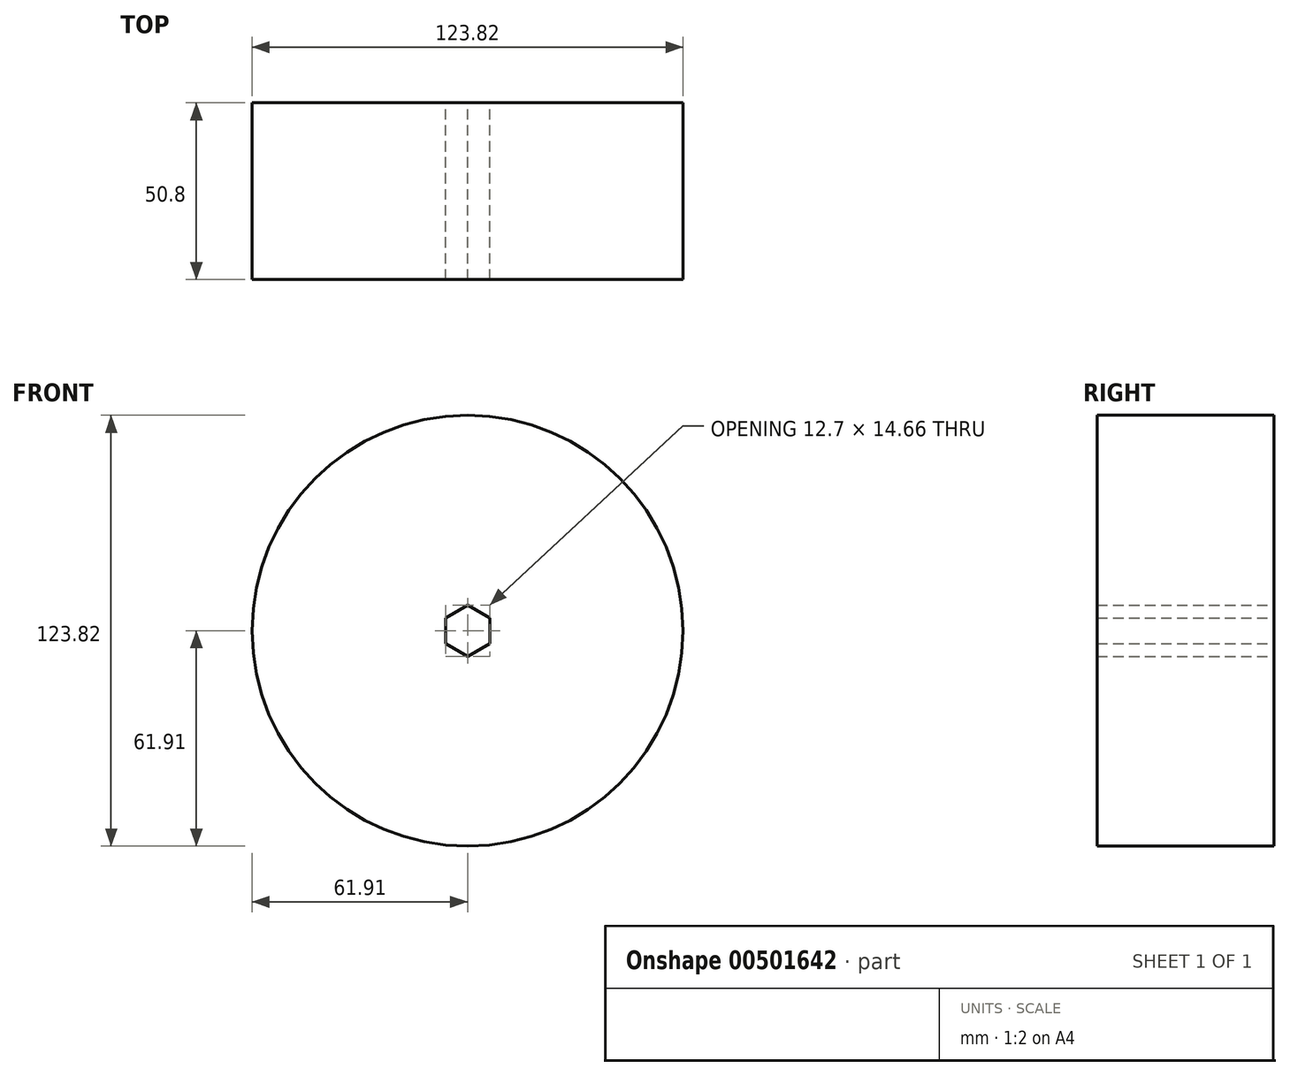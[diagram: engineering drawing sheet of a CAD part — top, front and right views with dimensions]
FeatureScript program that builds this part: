
annotation { "Feature Type Name" : "Feature", "Feature Type Description" : "" }
export const myFeature = defineFeature(function(context is Context, id is Id, definition is map)
    precondition{}
    {
        {
            var Q0;
            Q0=qCreatedBy(makeId("Front.planeOp"),FACE);
            var sketch = newSketch(context, id + "F0", { "sketchPlane" : qUnion([Q0])});
            skCircle(sketch, "E0", {"center": v(0, 0) * mm, "radius": 61.91 * mm});
            skCircle(sketch, "E1.cCircle", {"center": v(0, 0) * mm, "radius": 6.35 * mm, "construction": true});
            skLineSegment(sketch, "E1.0", {"start": v(-6.35, -3.67) * mm, "end": v(-6.35, 3.67) * mm});
            skLineSegment(sketch, "E1.1", {"start": v(-6.35, 3.67) * mm, "end": v(0, 7.33) * mm});
            skLineSegment(sketch, "E1.2", {"start": v(0, 7.33) * mm, "end": v(6.35, 3.67) * mm});
            skLineSegment(sketch, "E1.3", {"start": v(6.35, 3.67) * mm, "end": v(6.35, -3.67) * mm});
            skLineSegment(sketch, "E1.4", {"start": v(6.35, -3.67) * mm, "end": v(0, -7.33) * mm});
            skLineSegment(sketch, "E1.5", {"start": v(0, -7.33) * mm, "end": v(-6.35, -3.67) * mm});
            skPoint(sketch, "E1.0.midPoint", {"position": v(-6.35, 0) * mm});
            skSolve(sketch);
        }
        {
            var Q0;
            Q0=makeQuery(id+"F0.imprint","IMPRINT",FACE,{"disambiguationData":[TD([[makeQuery(id+"F0.imprint","IMPRINT",EDGE,{"derivedFrom":sQuery(id+"F0.wireOp",EDGE,"E0")}),1.0]])]});
            extrude(context, id + "F1", {"entities" : qUnion([Q0]), "depth" : 50.8 * mm});
        }
    });
